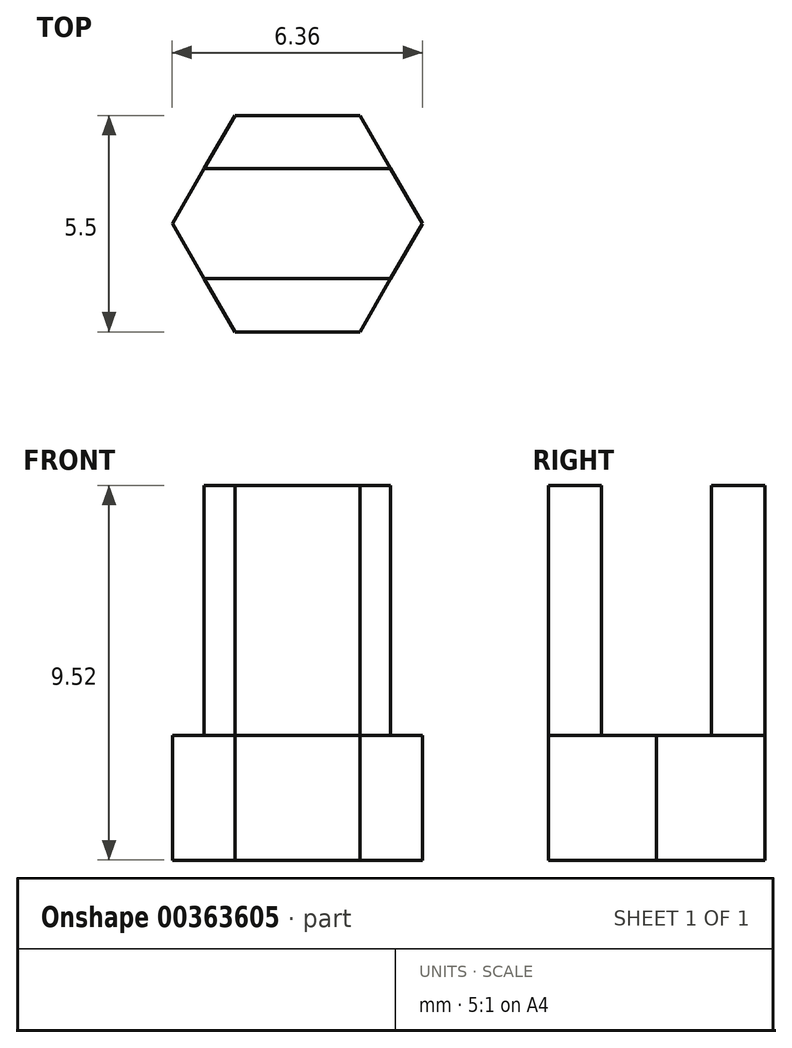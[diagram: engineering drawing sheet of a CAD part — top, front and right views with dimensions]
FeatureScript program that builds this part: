
annotation { "Feature Type Name" : "Feature", "Feature Type Description" : "" }
export const myFeature = defineFeature(function(context is Context, id is Id, definition is map)
    precondition{}
    {
        {
            var Q0;
            Q0=qCreatedBy(makeId("Top.planeOp"),FACE);
            var sketch = newSketch(context, id + "F0", { "sketchPlane" : qUnion([Q0])});
            skCircle(sketch, "E0.cCircle", {"center": v(0, 0) * mm, "radius": 2.75 * mm, "construction": true});
            skLineSegment(sketch, "E0.0", {"start": v(1.59, -2.75) * mm, "end": v(-1.59, -2.75) * mm});
            skLineSegment(sketch, "E0.1", {"start": v(-1.59, -2.75) * mm, "end": v(-3.18, 0) * mm});
            skLineSegment(sketch, "E0.2", {"start": v(-3.18, 0) * mm, "end": v(-1.59, 2.75) * mm});
            skLineSegment(sketch, "E0.3", {"start": v(-1.59, 2.75) * mm, "end": v(1.59, 2.75) * mm});
            skLineSegment(sketch, "E0.4", {"start": v(1.59, 2.75) * mm, "end": v(3.18, 0) * mm});
            skLineSegment(sketch, "E0.5", {"start": v(3.18, 0) * mm, "end": v(1.59, -2.75) * mm});
            skPoint(sketch, "E0.0.midPoint", {"position": v(0, -2.75) * mm});
            skSolve(sketch);
        }
        {
            var Q0;
            Q0 = qSketchRegion(id + "F0", true);
            extrude(context, id + "F1", {"entities" : qUnion([Q0]), "depth" : 12.7 * mm});
        }
        {
            var Q0;
            Q0=makeQuery(id+"F1.opExtrude","CAP_FACE",FACE,{"disambiguationData":[OSD([sQuery(id+"F0.wireOp",EDGE,"E0.0"),sQuery(id+"F0.wireOp",EDGE,"E0.1"),sQuery(id+"F0.wireOp",EDGE,"E0.2"),sQuery(id+"F0.wireOp",EDGE,"E0.3"),sQuery(id+"F0.wireOp",EDGE,"E0.4"),sQuery(id+"F0.wireOp",EDGE,"E0.5")])],"isStart":false});
            var sketch = newSketch(context, id + "F2", { "sketchPlane" : qUnion([Q0])});
            skLineSegment(sketch, "E1.bottom", {"start": v(-3.3, 1.4) * mm, "end": v(3.3, 1.4) * mm});
            skLineSegment(sketch, "E1.top", {"start": v(-3.3, -1.4) * mm, "end": v(3.3, -1.4) * mm});
            skLineSegment(sketch, "E1.left", {"start": v(-3.3, 1.4) * mm, "end": v(-3.3, -1.4) * mm});
            skLineSegment(sketch, "E1.right", {"start": v(3.3, 1.4) * mm, "end": v(3.3, -1.4) * mm});
            skSolve(sketch);
        }
        {
            var Q0;
            Q0 = qSketchRegion(id + "F2", true);
            extrude(context, id + "F3", {"entities" : qUnion([Q0]), "operationType" : NewBodyOperationType.REMOVE, "endBound" : BoundingType.THROUGH_ALL, "oppositeDirection" : true, "depth" : 25.4 * mm});
        }
        {
            var Q0;
            Q0=makeQuery(id+"F1.opExtrude","CAP_FACE",FACE,{"disambiguationData":[OSD([sQuery(id+"F0.wireOp",EDGE,"E0.0"),sQuery(id+"F0.wireOp",EDGE,"E0.1"),sQuery(id+"F0.wireOp",EDGE,"E0.2"),sQuery(id+"F0.wireOp",EDGE,"E0.3"),sQuery(id+"F0.wireOp",EDGE,"E0.4"),sQuery(id+"F0.wireOp",EDGE,"E0.5")])],"isStart":false});
            var sketch = newSketch(context, id + "F4", { "sketchPlane" : qUnion([Q0])});
            skCircle(sketch, "E2", {"center": v(0, 0) * mm, "radius": 3.43 * mm});
            skSolve(sketch);
        }
        {
            var Q0;
            Q0 = qSketchRegion(id + "F4", true);
            extrude(context, id + "F5", {"entities" : qUnion([Q0]), "operationType" : NewBodyOperationType.REMOVE, "oppositeDirection" : true, "depth" : 6.35 * mm});
        }
        {
            var Q0;
            {var subQ0=sQuery(id+"F0.wireOp",EDGE,"E0.0");var subQ1=sQuery(id+"F0.wireOp",EDGE,"E0.1");var subQ2=sQuery(id+"F0.wireOp",EDGE,"E0.5");Q0=makeQuery(id+"F3.boolean.opBoolean","SPLIT",FACE,{"disambiguationData":[TD([makeQuery(id+"F1.opExtrude","SWEPT_FACE",FACE,{"disambiguationData":[OSD([subQ0])]})])],"derivedFrom":makeQuery(id+"F1.opExtrude","CAP_FACE",FACE,{"disambiguationData":[OSD([subQ0,subQ1,sQuery(id+"F0.wireOp",EDGE,"E0.2"),sQuery(id+"F0.wireOp",EDGE,"E0.3"),sQuery(id+"F0.wireOp",EDGE,"E0.4"),subQ2])],"isStart":true})});}
            var sketch = newSketch(context, id + "F6", { "sketchPlane" : qUnion([Q0])});
            skCircle(sketch, "E3.cCircle", {"center": v(0, 0) * mm, "radius": 2.75 * mm, "construction": true});
            skLineSegment(sketch, "E3.0", {"start": v(-1.59, 2.75) * mm, "end": v(1.59, 2.75) * mm});
            skLineSegment(sketch, "E3.1", {"start": v(1.59, 2.75) * mm, "end": v(3.17, 0) * mm});
            skLineSegment(sketch, "E3.2", {"start": v(3.17, 0) * mm, "end": v(1.59, -2.75) * mm});
            skLineSegment(sketch, "E3.3", {"start": v(1.59, -2.75) * mm, "end": v(-1.59, -2.75) * mm});
            skLineSegment(sketch, "E3.4", {"start": v(-1.59, -2.75) * mm, "end": v(-3.17, 0) * mm});
            skLineSegment(sketch, "E3.5", {"start": v(-3.17, 0) * mm, "end": v(-1.59, 2.75) * mm});
            skPoint(sketch, "E3.0.midPoint", {"position": v(0, 2.75) * mm});
            skSolve(sketch);
        }
        {
            var Q0;
            Q0 = qSketchRegion(id + "F6", true);
            extrude(context, id + "F7", {"entities" : qUnion([Q0]), "depth" : 3.17 * mm});
        }
    });
